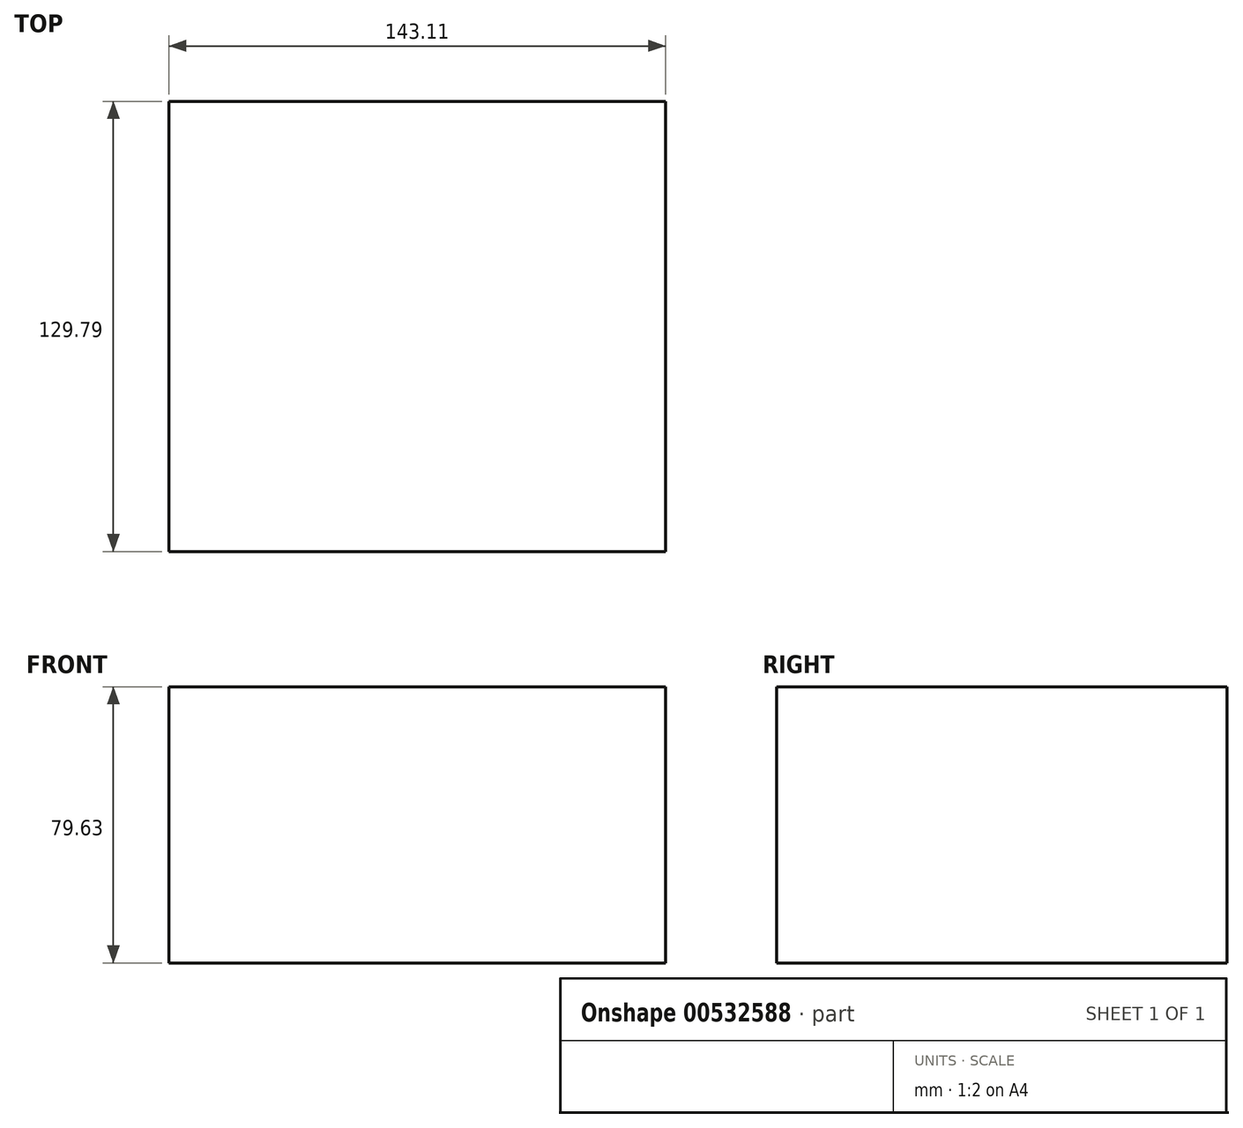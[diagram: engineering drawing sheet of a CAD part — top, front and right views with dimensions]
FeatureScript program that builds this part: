
annotation { "Feature Type Name" : "Feature", "Feature Type Description" : "" }
export const myFeature = defineFeature(function(context is Context, id is Id, definition is map)
    precondition{}
    {
        {
            var Q0;
            Q0=qCreatedBy(makeId("Front.planeOp"),FACE);
            var sketch = newSketch(context, id + "F0", { "sketchPlane" : qUnion([Q0])});
            skLineSegment(sketch, "E0.bottom", {"start": v(-61.39, -16.94) * mm, "end": v(81.72, -16.94) * mm});
            skLineSegment(sketch, "E0.top", {"start": v(-61.39, 62.7) * mm, "end": v(81.72, 62.7) * mm});
            skLineSegment(sketch, "E0.left", {"start": v(-61.39, -16.94) * mm, "end": v(-61.39, 62.7) * mm});
            skLineSegment(sketch, "E0.right", {"start": v(81.72, -16.94) * mm, "end": v(81.72, 62.7) * mm});
            skSolve(sketch);
        }
        {
            var Q0;
            Q0=makeQuery(id+"F0.imprint","IMPRINT",FACE,{"disambiguationData":[TD([[makeQuery(id+"F0.imprint","IMPRINT",EDGE,{"derivedFrom":sQuery(id+"F0.wireOp",EDGE,"E0.bottom")}),1.0]])]});
            extrude(context, id + "F1", {"entities" : qUnion([Q0]), "depth" : 129.8 * mm, "offsetDistance" : 25.4 * mm});
        }
    });
